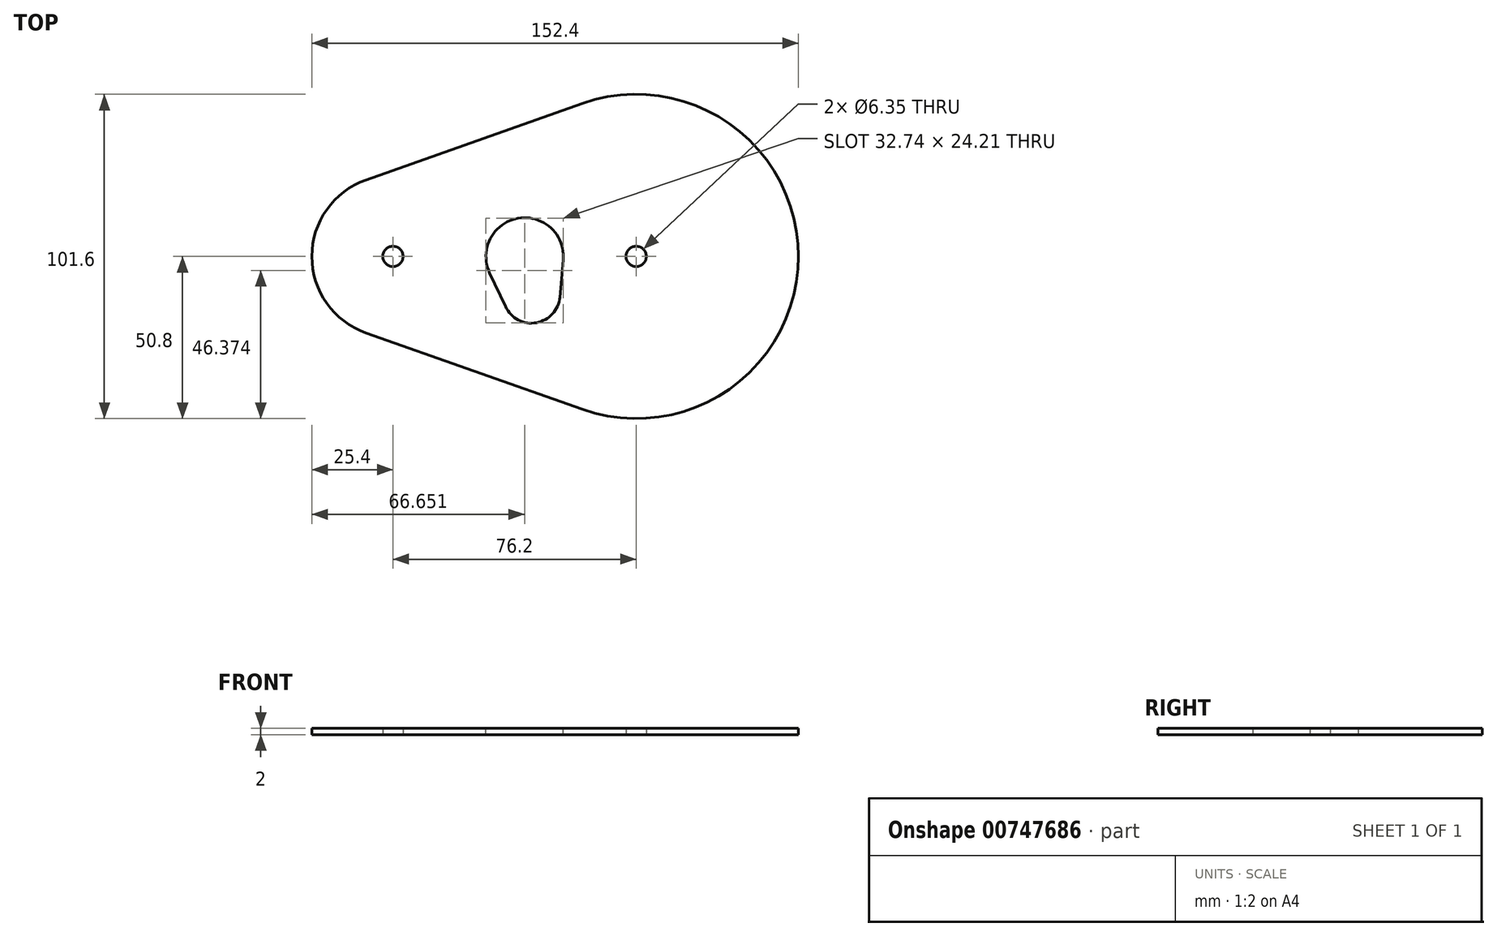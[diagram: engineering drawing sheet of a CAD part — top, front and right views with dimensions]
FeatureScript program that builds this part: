
annotation { "Feature Type Name" : "Feature", "Feature Type Description" : "" }
export const myFeature = defineFeature(function(context is Context, id is Id, definition is map)
    precondition{}
    {
        {
            var Q0;
            Q0=qCreatedBy(makeId("Top.planeOp"),FACE);
            var sketch = newSketch(context, id + "F0", { "sketchPlane" : qUnion([Q0])});
            skArc(sketch, "E0", {"start": v(-16.93, -47.9) * mm, "mid": v(50.8, 0) * mm, "end": v(-16.93, 47.9) * mm});
            skArc(sketch, "E1", {"start": v(-84.67, 23.95) * mm, "mid": v(-101.6, 0) * mm, "end": v(-84.67, -23.95) * mm});
            skLineSegment(sketch, "E2", {"start": v(-84.67, -23.95) * mm, "end": v(-16.93, -47.9) * mm});
            skLineSegment(sketch, "E3", {"start": v(-84.67, 23.95) * mm, "end": v(-16.93, 47.9) * mm});
            skCircle(sketch, "E4", {"center": v(0, 0) * mm, "radius": 3.18 * mm});
            skCircle(sketch, "E5", {"center": v(-76.2, 0) * mm, "radius": 3.18 * mm});
            skSolve(sketch);
        }
        {
            var Q0;
            Q0 = qSketchRegion(id + "F0", true);
            extrude(context, id + "F1", {"entities" : qUnion([Q0]), "depth" : 2 * mm, "offsetDistance" : 25.4 * mm});
        }
        {
            var Q0;
            Q0=makeQuery(id+"F1.opExtrude","CAP_FACE",FACE,{"disambiguationData":[OSD([sQuery(id+"F0.wireOp",EDGE,"E0"),sQuery(id+"F0.wireOp",EDGE,"E1"),sQuery(id+"F0.wireOp",EDGE,"E2"),sQuery(id+"F0.wireOp",EDGE,"E3"),sQuery(id+"F0.wireOp",EDGE,"E4"),sQuery(id+"F0.wireOp",EDGE,"E5")])],"isStart":false});
            var sketch = newSketch(context, id + "F2", { "sketchPlane" : qUnion([Q0])});
            skCircle(sketch, "E6", {"center": v(0, 0) * mm, "radius": 34.93 * mm});
            skArc(sketch, "E7", {"start": v(-22.84, -1.1) * mm, "mid": v(-37.03, 11.95) * mm, "end": v(-45.9, -5.16) * mm});
            skArc(sketch, "E8", {"start": v(-40.92, -15.75) * mm, "mid": v(-31.26, -20.76) * mm, "end": v(-23.9, -12.75) * mm});
            skLineSegment(sketch, "E9", {"start": v(-45.9, -5.16) * mm, "end": v(-40.92, -15.75) * mm});
            skLineSegment(sketch, "E10", {"start": v(-22.84, -1.1) * mm, "end": v(-23.9, -12.75) * mm});
            skSolve(sketch);
        }
        {
            var Q0;
            {var subQ5=sQuery(id+"F2.wireOp",EDGE,"E9");Q0=makeQuery(id+"F2.imprint","IMPRINT",FACE,{"disambiguationData":[TD([[makeQuery(id+"F2.imprint","IMPRINT",EDGE,{"derivedFrom":subQ5}),1.0]])]});}
            var Q1;
            {var subQ5=sQuery(id+"F2.wireOp",EDGE,"E10");Q1=makeQuery(id+"F2.imprint","IMPRINT",FACE,{"disambiguationData":[TD([[makeQuery(id+"F2.imprint","IMPRINT",EDGE,{"derivedFrom":subQ5}),-1.0]])]});}
            extrude(context, id + "F3", {"entities" : qUnion([Q0, Q1]), "operationType" : NewBodyOperationType.REMOVE, "endBound" : BoundingType.THROUGH_ALL, "oppositeDirection" : true, "depth" : 25.4 * mm, "offsetDistance" : 25.4 * mm});
        }
        {
            var Q0;
            Q0=qCreatedBy(makeId("Right.planeOp"),FACE);
            var sketch = newSketch(context, id + "F4", { "sketchPlane" : qUnion([Q0])});
            skLineSegment(sketch, "E11", {"start": v(0, -19.48) * mm, "end": v(0, 32.36) * mm});
            skSolve(sketch);
        }
    });
